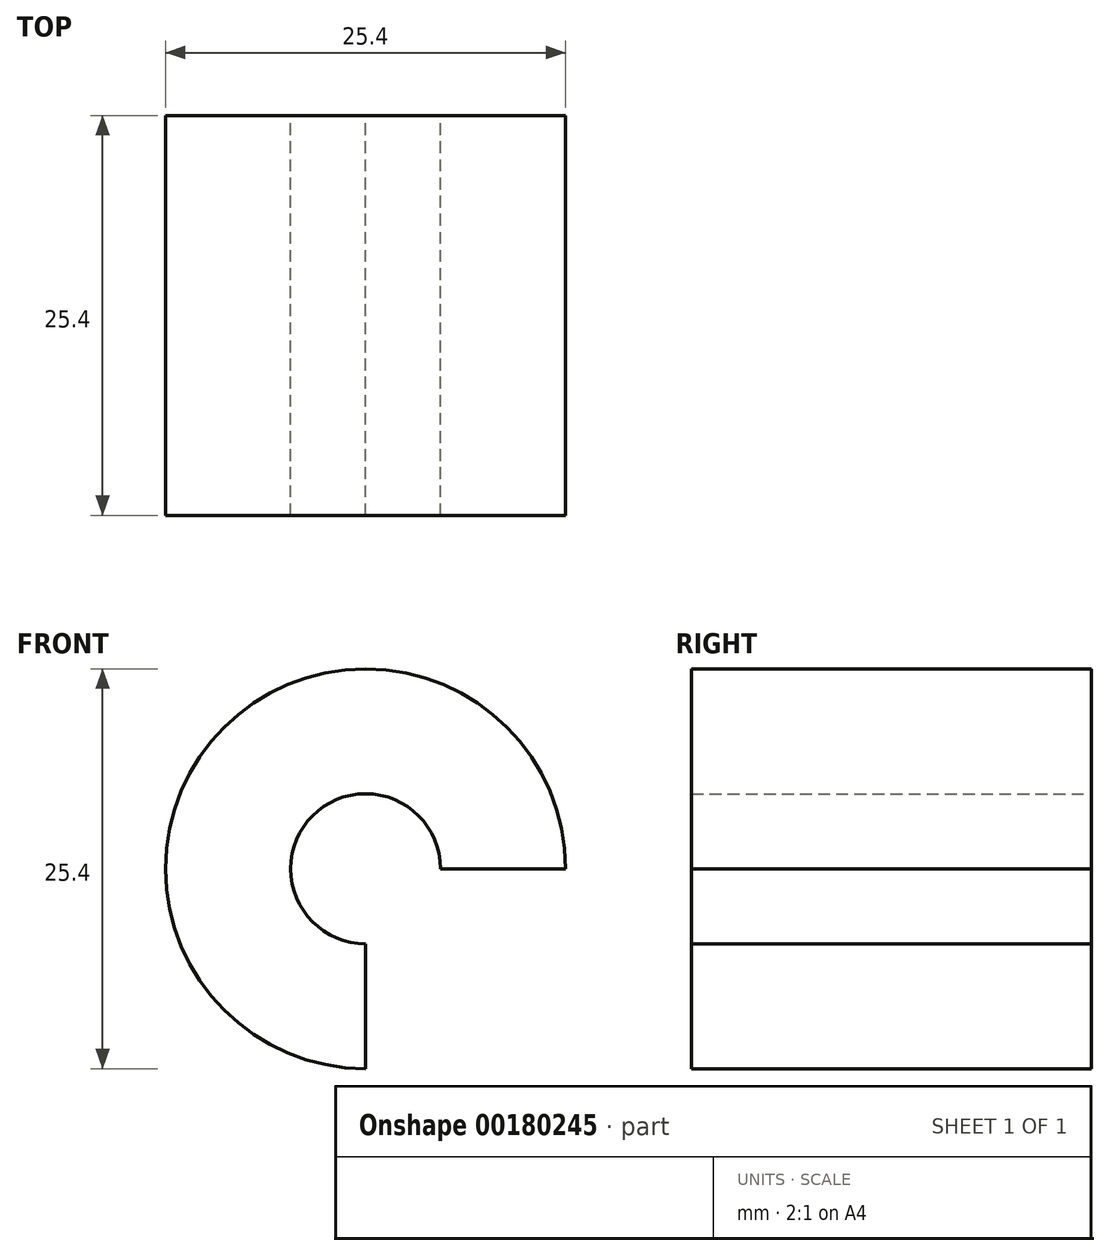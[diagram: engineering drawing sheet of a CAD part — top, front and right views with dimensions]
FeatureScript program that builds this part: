
annotation { "Feature Type Name" : "Feature", "Feature Type Description" : "" }
export const myFeature = defineFeature(function(context is Context, id is Id, definition is map)
    precondition{}
    {
        {
            var Q0;
            Q0=qCreatedBy(makeId("Front.planeOp"),FACE);
            var sketch = newSketch(context, id + "F0", { "sketchPlane" : qUnion([Q0])});
            skArc(sketch, "E0", {"start": v(12.7, 0) * mm, "mid": v(-8.98, 8.98) * mm, "end": v(0, -12.7) * mm});
            skArc(sketch, "E1", {"start": v(4.76, 0) * mm, "mid": v(-3.37, 3.37) * mm, "end": v(0, -4.76) * mm});
            skLineSegment(sketch, "E2", {"start": v(4.76, 0) * mm, "end": v(12.7, 0) * mm});
            skLineSegment(sketch, "E3", {"start": v(0, -4.76) * mm, "end": v(0, -12.7) * mm});
            skSolve(sketch);
        }
        {
            var Q0;
            Q0=makeQuery(id+"F0.imprint","IMPRINT",FACE,{"disambiguationData":[TD([[makeQuery(id+"F0.imprint","IMPRINT",EDGE,{"derivedFrom":sQuery(id+"F0.wireOp",EDGE,"E0")}),1.0]])]});
            extrude(context, id + "F1", {"entities" : qUnion([Q0]), "depth" : 25.4 * mm});
        }
    });
